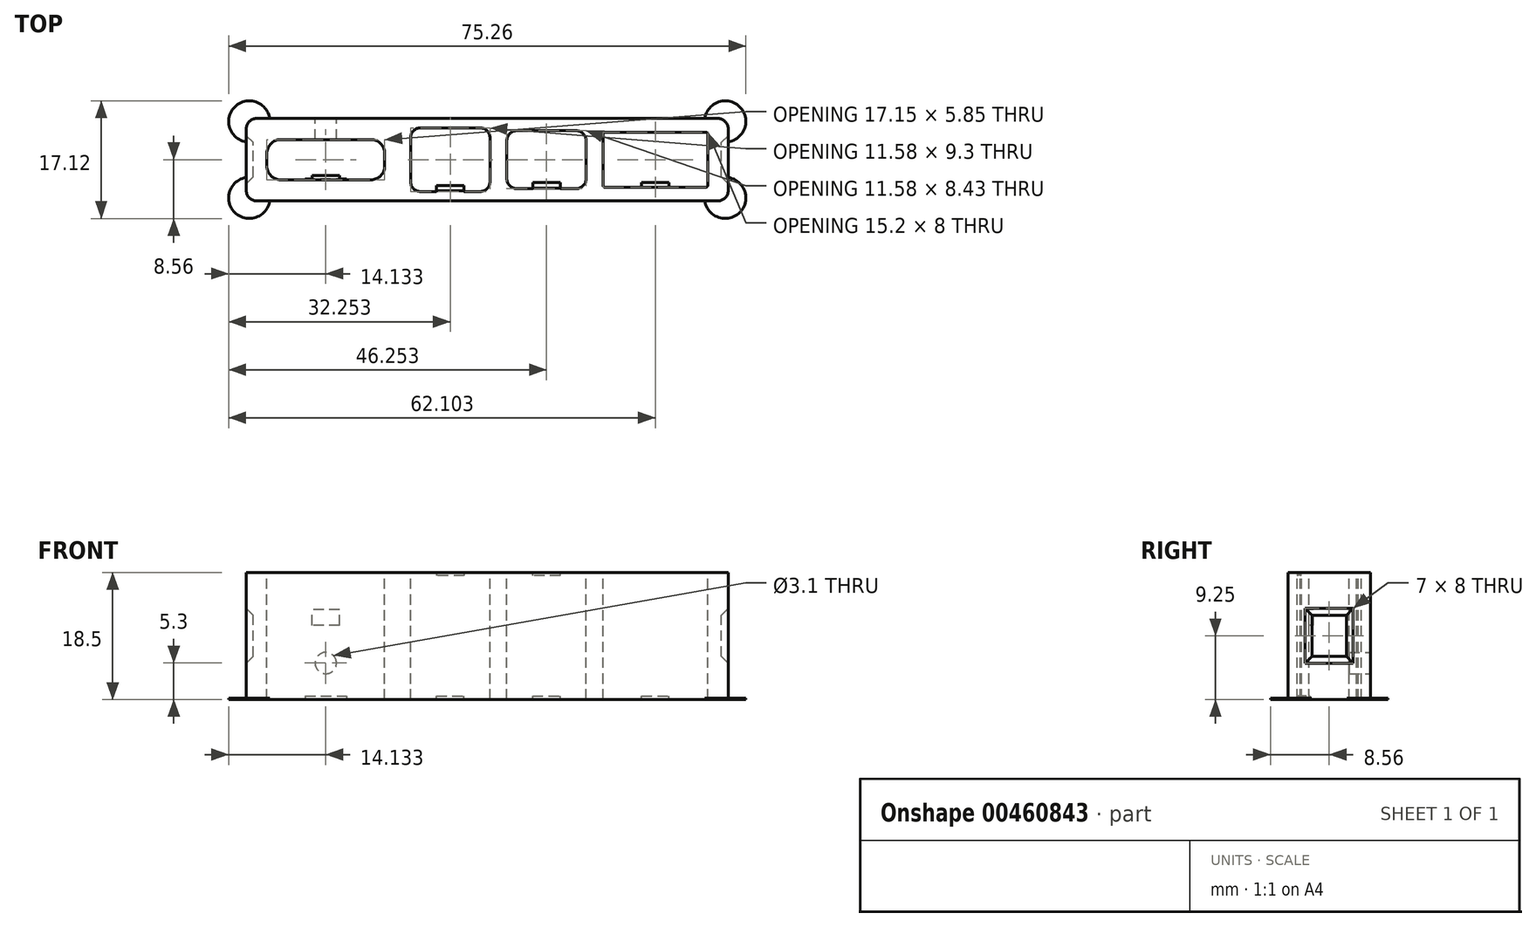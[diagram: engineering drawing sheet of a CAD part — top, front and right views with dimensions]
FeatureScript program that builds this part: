
annotation { "Feature Type Name" : "Feature", "Feature Type Description" : "" }
export const myFeature = defineFeature(function(context is Context, id is Id, definition is map)
    precondition{}
    {
        {
            assignVariable(context, id + "F0", {"name" : "TB1CableStopHeight", "anyValue" : .1});
        }
        {
            var Q0;
            Q0=qCreatedBy(makeId("Front.planeOp"),FACE);
            var sketch = newSketch(context, id + "F1", { "sketchPlane" : qUnion([Q0])});
            skLineSegment(sketch, "E0.bottom", {"start": v(33.57, -6) * mm, "end": v(-33.57, -6) * mm});
            skLineSegment(sketch, "E0.top", {"start": v(33.57, 6) * mm, "end": v(-33.57, 6) * mm});
            skLineSegment(sketch, "E0.left", {"start": v(35.07, -4.5) * mm, "end": v(35.07, 4.5) * mm});
            skLineSegment(sketch, "E0.right", {"start": v(-35.07, -4.5) * mm, "end": v(-35.07, 4.5) * mm});
            skPoint(sketch, "E0.middle", {"position": v(0, 0) * mm});
            skLineSegment(sketch, "E1", {"start": v(-35.07, 0) * mm, "end": v(35.07, 0) * mm, "construction": true});
            skLineSegment(sketch, "E2.bottom", {"start": v(-16.92, -2.92) * mm, "end": v(-30.07, -2.92) * mm});
            skLineSegment(sketch, "E2.top", {"start": v(-16.92, 2.93) * mm, "end": v(-30.07, 2.93) * mm});
            skLineSegment(sketch, "E2.left", {"start": v(-14.92, -0.92) * mm, "end": v(-14.92, 0.93) * mm});
            skLineSegment(sketch, "E2.right", {"start": v(-32.07, -0.92) * mm, "end": v(-32.07, 0.93) * mm});
            skPoint(sketch, "E2.middle", {"position": v(-23.5, 0) * mm});
            skLineSegment(sketch, "E3.bottom", {"start": v(-1.09, 4.65) * mm, "end": v(-9.67, 4.65) * mm});
            skLineSegment(sketch, "E3.top", {"start": v(-1.09, -4.65) * mm, "end": v(-9.67, -4.65) * mm});
            skLineSegment(sketch, "E3.left", {"start": v(0.41, 3.15) * mm, "end": v(0.41, -3.15) * mm});
            skLineSegment(sketch, "E3.right", {"start": v(-11.17, 3.15) * mm, "end": v(-11.17, -3.15) * mm});
            skPoint(sketch, "E3.middle", {"position": v(-5.38, 0) * mm});
            skLineSegment(sketch, "E4.bottom", {"start": v(12.91, 4.21) * mm, "end": v(4.33, 4.21) * mm});
            skLineSegment(sketch, "E4.top", {"start": v(12.91, -4.21) * mm, "end": v(4.33, -4.22) * mm});
            skLineSegment(sketch, "E4.left", {"start": v(14.41, 2.72) * mm, "end": v(14.41, -2.72) * mm});
            skLineSegment(sketch, "E4.right", {"start": v(2.83, 2.71) * mm, "end": v(2.83, -2.72) * mm});
            skPoint(sketch, "E4.middle", {"position": v(8.62, 0) * mm});
            skLineSegment(sketch, "E5.bottom", {"start": v(31.87, -4) * mm, "end": v(17.07, -4) * mm});
            skLineSegment(sketch, "E5.top", {"start": v(31.87, 4) * mm, "end": v(17.07, 4) * mm});
            skLineSegment(sketch, "E5.left", {"start": v(32.07, -3.8) * mm, "end": v(32.07, 3.8) * mm});
            skLineSegment(sketch, "E5.right", {"start": v(16.87, -3.8) * mm, "end": v(16.87, 3.8) * mm});
            skPoint(sketch, "E5.middle", {"position": v(24.47, 0) * mm});
            skPoint(sketch, "E6.visualSharp", {"position": v(-32.07, 2.93) * mm});
            skArc(sketch, "E6.filletArc", {"start": v(-30.07, 2.93) * mm, "mid": v(-31.49, 2.34) * mm, "end": v(-32.07, 0.93) * mm});
            skPoint(sketch, "E7.visualSharp", {"position": v(-14.92, 2.93) * mm});
            skArc(sketch, "E7.filletArc", {"start": v(-14.92, 0.93) * mm, "mid": v(-15.5, 2.34) * mm, "end": v(-16.92, 2.93) * mm});
            skPoint(sketch, "E8.visualSharp", {"position": v(-14.92, -2.92) * mm});
            skArc(sketch, "E8.filletArc", {"start": v(-16.92, -2.92) * mm, "mid": v(-15.5, -2.34) * mm, "end": v(-14.92, -0.92) * mm});
            skPoint(sketch, "E9.visualSharp", {"position": v(-32.07, -2.93) * mm});
            skArc(sketch, "E9.filletArc", {"start": v(-32.07, -0.92) * mm, "mid": v(-31.49, -2.34) * mm, "end": v(-30.07, -2.92) * mm});
            skPoint(sketch, "E10.visualSharp", {"position": v(-11.17, 4.65) * mm});
            skArc(sketch, "E10.filletArc", {"start": v(-9.67, 4.65) * mm, "mid": v(-10.73, 4.21) * mm, "end": v(-11.17, 3.15) * mm});
            skPoint(sketch, "E11.visualSharp", {"position": v(0.41, 4.65) * mm});
            skArc(sketch, "E11.filletArc", {"start": v(0.41, 3.15) * mm, "mid": v(-0.03, 4.21) * mm, "end": v(-1.09, 4.65) * mm});
            skPoint(sketch, "E12.visualSharp", {"position": v(-11.17, -4.65) * mm});
            skArc(sketch, "E12.filletArc", {"start": v(-11.17, -3.15) * mm, "mid": v(-10.73, -4.21) * mm, "end": v(-9.67, -4.65) * mm});
            skPoint(sketch, "E13.visualSharp", {"position": v(0.41, -4.65) * mm});
            skArc(sketch, "E13.filletArc", {"start": v(-1.09, -4.65) * mm, "mid": v(-0.03, -4.21) * mm, "end": v(0.41, -3.15) * mm});
            skPoint(sketch, "E14.visualSharp", {"position": v(2.83, 4.21) * mm});
            skArc(sketch, "E14.filletArc", {"start": v(4.33, 4.21) * mm, "mid": v(3.27, 3.78) * mm, "end": v(2.83, 2.71) * mm});
            skPoint(sketch, "E15.visualSharp", {"position": v(14.41, 4.21) * mm});
            skArc(sketch, "E15.filletArc", {"start": v(14.41, 2.72) * mm, "mid": v(13.97, 3.78) * mm, "end": v(12.91, 4.21) * mm});
            skPoint(sketch, "E16.visualSharp", {"position": v(14.41, -4.21) * mm});
            skArc(sketch, "E16.filletArc", {"start": v(12.91, -4.22) * mm, "mid": v(13.97, -3.78) * mm, "end": v(14.41, -2.72) * mm});
            skPoint(sketch, "E17.visualSharp", {"position": v(2.83, -4.22) * mm});
            skArc(sketch, "E17.filletArc", {"start": v(2.83, -2.72) * mm, "mid": v(3.27, -3.78) * mm, "end": v(4.33, -4.22) * mm});
            skPoint(sketch, "E18.visualSharp", {"position": v(16.87, 4) * mm});
            skArc(sketch, "E18.filletArc", {"start": v(17.07, 4) * mm, "mid": v(16.93, 3.94) * mm, "end": v(16.87, 3.8) * mm});
            skPoint(sketch, "E19.visualSharp", {"position": v(32.07, 4) * mm});
            skArc(sketch, "E19.filletArc", {"start": v(32.07, 3.8) * mm, "mid": v(32.01, 3.94) * mm, "end": v(31.87, 4) * mm});
            skPoint(sketch, "E20.visualSharp", {"position": v(32.07, -4) * mm});
            skArc(sketch, "E20.filletArc", {"start": v(31.87, -4) * mm, "mid": v(32.01, -3.94) * mm, "end": v(32.07, -3.8) * mm});
            skPoint(sketch, "E21.visualSharp", {"position": v(16.87, -4) * mm});
            skArc(sketch, "E21.filletArc", {"start": v(16.87, -3.8) * mm, "mid": v(16.93, -3.94) * mm, "end": v(17.07, -4) * mm});
            skPoint(sketch, "E22.visualSharp", {"position": v(-35.07, 6) * mm});
            skArc(sketch, "E22.filletArc", {"start": v(-33.57, 6) * mm, "mid": v(-34.63, 5.56) * mm, "end": v(-35.07, 4.5) * mm});
            skPoint(sketch, "E23.visualSharp", {"position": v(35.07, 6) * mm});
            skArc(sketch, "E23.filletArc", {"start": v(35.07, 4.5) * mm, "mid": v(34.63, 5.56) * mm, "end": v(33.57, 6) * mm});
            skPoint(sketch, "E24.visualSharp", {"position": v(35.07, -6) * mm});
            skArc(sketch, "E24.filletArc", {"start": v(33.57, -6) * mm, "mid": v(34.63, -5.56) * mm, "end": v(35.07, -4.5) * mm});
            skPoint(sketch, "E25.visualSharp", {"position": v(-35.07, -6) * mm});
            skArc(sketch, "E25.filletArc", {"start": v(-35.07, -4.5) * mm, "mid": v(-34.63, -5.56) * mm, "end": v(-33.57, -6) * mm});
            skSolve(sketch);
        }
        {
            var Q0;
            Q0=makeQuery(id+"F1.imprint","IMPRINT",FACE,{"disambiguationData":[TD([[makeQuery(id+"F1.imprint","IMPRINT",EDGE,{"derivedFrom":sQuery(id+"F1.wireOp",EDGE,"E0.bottom")}),-1.0]])]});
            extrude(context, id + "F2", {"entities" : qUnion([Q0]), "oppositeDirection" : true, "depth" : 18.5 * mm});
        }
        {
            var Q0;
            Q0=makeQuery(id+"F2.opExtrude","SWEPT_FACE",FACE,{"disambiguationData":[OSD([sQuery(id+"F1.wireOp",EDGE,"E0.top")])]});
            var sketch = newSketch(context, id + "F3", { "sketchPlane" : qUnion([Q0])});
            skPoint(sketch, "E26.0", {"position": v(-23.5, 0) * mm});
            skCircle(sketch, "E27", {"center": v(-23.5, 13.2) * mm, "radius": 1.55 * mm});
            skPoint(sketch, "E28.0", {"position": v(33.57, 9.25) * mm});
            skLineSegment(sketch, "E29.bottom", {"start": v(3.5, 13.25) * mm, "end": v(-3.5, 13.25) * mm});
            skLineSegment(sketch, "E29.top", {"start": v(3.5, 5.25) * mm, "end": v(-3.5, 5.25) * mm});
            skLineSegment(sketch, "E29.left", {"start": v(3.5, 13.25) * mm, "end": v(3.5, 5.25) * mm});
            skLineSegment(sketch, "E29.right", {"start": v(-3.5, 13.25) * mm, "end": v(-3.5, 5.25) * mm});
            skPoint(sketch, "E29.middle", {"position": v(0, 9.25) * mm});
            skSolve(sketch);
        }
        {
            var Q0;
            Q0=makeQuery(id+"F3.imprint","IMPRINT",FACE,{"disambiguationData":[TD([[makeQuery(id+"F3.imprint","IMPRINT",EDGE,{"derivedFrom":sQuery(id+"F3.wireOp",EDGE,"E27")}),1.0]])]});
            extrude(context, id + "F4", {"entities" : qUnion([Q0]), "operationType" : NewBodyOperationType.REMOVE, "endBound" : BoundingType.UP_TO_NEXT, "oppositeDirection" : true, "depth" : 25 * mm});
        }
        {
            var Q0;
            Q0=makeQuery(id+"F2.opExtrude","SWEPT_FACE",FACE,{"disambiguationData":[OSD([sQuery(id+"F1.wireOp",EDGE,"E2.bottom")])]});
            var sketch = newSketch(context, id + "F5", { "sketchPlane" : qUnion([Q0])});
            skPoint(sketch, "E30.0", {"position": v(-23.5, 0) * mm});
            skLineSegment(sketch, "E31.bottom", {"start": v(-26.5, 18) * mm, "end": v(-20.5, 18) * mm});
            skLineSegment(sketch, "E31.top", {"start": v(-26.5, 18.5) * mm, "end": v(-20.5, 18.5) * mm});
            skLineSegment(sketch, "E31.left", {"start": v(-26.5, 18) * mm, "end": v(-26.5, 18.5) * mm});
            skLineSegment(sketch, "E31.right", {"start": v(-20.5, 18) * mm, "end": v(-20.5, 18.5) * mm});
            skPoint(sketch, "E31.middle", {"position": v(-23.5, 18.25) * mm});
            skLineSegment(sketch, "E32.0", {"start": v(-16.92, 18.5) * mm, "end": v(-30.07, 18.5) * mm});
            skLineSegment(sketch, "E33.bottom", {"start": v(-21.5, 7.7) * mm, "end": v(-25.5, 7.7) * mm});
            skLineSegment(sketch, "E33.top", {"start": v(-21.5, 5.45) * mm, "end": v(-25.5, 5.45) * mm});
            skLineSegment(sketch, "E33.left", {"start": v(-21.5, 7.7) * mm, "end": v(-21.5, 5.45) * mm});
            skLineSegment(sketch, "E33.right", {"start": v(-25.5, 7.7) * mm, "end": v(-25.5, 5.45) * mm});
            skPoint(sketch, "E33.middle", {"position": v(-23.5, 6.57) * mm});
            skSolve(sketch);
        }
        {
            var Q0;
            Q0=makeQuery(id+"F5.imprint","IMPRINT",FACE,{"disambiguationData":[TD([[makeQuery(id+"F5.imprint","IMPRINT",EDGE,{"derivedFrom":sQuery(id+"F5.wireOp",EDGE,"E31.bottom")}),1.0]])]});
            extrude(context, id + "F6", {"entities" : qUnion([Q0]), "operationType" : NewBodyOperationType.ADD, "depth" : .1 * mm});
        }
        {
            var Q0;
            Q0=makeQuery(id+"F5.imprint","IMPRINT",FACE,{"disambiguationData":[TD([[makeQuery(id+"F5.imprint","IMPRINT",EDGE,{"derivedFrom":sQuery(id+"F5.wireOp",EDGE,"E33.bottom")}),1.0]])]});
            extrude(context, id + "F7", {"entities" : qUnion([Q0]), "operationType" : NewBodyOperationType.ADD, "depth" : .6 * mm});
        }
        {
            var Q0;
            Q0=makeQuery(id+"F2.opExtrude","SWEPT_FACE",FACE,{"disambiguationData":[OSD([sQuery(id+"F1.wireOp",EDGE,"E3.top")])]});
            var sketch = newSketch(context, id + "F8", { "sketchPlane" : qUnion([Q0])});
            skPoint(sketch, "E34.0", {"position": v(-5.38, 0) * mm});
            skLineSegment(sketch, "E35.bottom", {"start": v(-7.38, 18.5) * mm, "end": v(-3.38, 18.5) * mm});
            skLineSegment(sketch, "E35.top", {"start": v(-7.38, 18) * mm, "end": v(-3.38, 18) * mm});
            skLineSegment(sketch, "E35.left", {"start": v(-7.38, 18.5) * mm, "end": v(-7.38, 18) * mm});
            skLineSegment(sketch, "E35.right", {"start": v(-3.38, 18.5) * mm, "end": v(-3.38, 18) * mm});
            skPoint(sketch, "E35.middle", {"position": v(-5.38, 18.25) * mm});
            skLineSegment(sketch, "E36.bottom", {"start": v(-3.38, -1.03) * mm, "end": v(-7.38, -1.03) * mm});
            skLineSegment(sketch, "E36.top", {"start": v(-3.38, 0.47) * mm, "end": v(-7.38, 0.47) * mm});
            skLineSegment(sketch, "E36.left", {"start": v(-3.38, -1.03) * mm, "end": v(-3.38, 0.47) * mm});
            skLineSegment(sketch, "E36.right", {"start": v(-7.38, -1.03) * mm, "end": v(-7.38, 0.47) * mm});
            skPoint(sketch, "E36.middle", {"position": v(-5.38, -0.28) * mm});
            skLineSegment(sketch, "E37.0", {"start": v(-1.09, 18.5) * mm, "end": v(-9.67, 18.5) * mm});
            skSolve(sketch);
        }
        {
            var Q0;
            Q0=makeQuery(id+"F8.imprint","IMPRINT",FACE,{"disambiguationData":[TD([[makeQuery(id+"F8.imprint","IMPRINT",EDGE,{"derivedFrom":sQuery(id+"F8.wireOp",EDGE,"E35.top")}),1.0]])]});
            extrude(context, id + "F9", {"entities" : qUnion([Q0]), "operationType" : NewBodyOperationType.ADD, "depth" : .9 * mm});
        }
        {
            var Q0;
            {var subQ0=sQuery(id+"F8.wireOp",EDGE,"E36.top");Q0=makeQuery(id+"F8.imprint","IMPRINT",FACE,{"disambiguationData":[TD([[makeQuery(id+"F8.imprint","IMPRINT",EDGE,{"derivedFrom":subQ0}),1.0]])]});}
            extrude(context, id + "F10", {"entities" : qUnion([Q0]), "operationType" : NewBodyOperationType.ADD, "depth" : (getVariable(context, 'TB1CableStopHeight')) * mm});
        }
        {
            var Q0;
            Q0=makeQuery(id+"F2.opExtrude","SWEPT_FACE",FACE,{"disambiguationData":[OSD([sQuery(id+"F1.wireOp",EDGE,"E4.top")])]});
            var sketch = newSketch(context, id + "F11", { "sketchPlane" : qUnion([Q0])});
            skPoint(sketch, "E38.0", {"position": v(8.62, 0) * mm});
            skLineSegment(sketch, "E39.bottom", {"start": v(6.62, 18.5) * mm, "end": v(10.62, 18.5) * mm});
            skLineSegment(sketch, "E39.top", {"start": v(6.62, 18) * mm, "end": v(10.62, 18) * mm});
            skLineSegment(sketch, "E39.left", {"start": v(6.62, 18.5) * mm, "end": v(6.62, 18) * mm});
            skLineSegment(sketch, "E39.right", {"start": v(10.62, 18.5) * mm, "end": v(10.62, 18) * mm});
            skPoint(sketch, "E39.middle", {"position": v(8.62, 18.25) * mm});
            skLineSegment(sketch, "E40.bottom", {"start": v(10.62, 0.47) * mm, "end": v(6.62, 0.47) * mm});
            skLineSegment(sketch, "E40.top", {"start": v(10.62, -1.03) * mm, "end": v(6.62, -1.03) * mm});
            skLineSegment(sketch, "E40.left", {"start": v(10.62, 0.47) * mm, "end": v(10.62, -1.03) * mm});
            skLineSegment(sketch, "E40.right", {"start": v(6.62, 0.47) * mm, "end": v(6.62, -1.03) * mm});
            skPoint(sketch, "E40.middle", {"position": v(8.62, -0.28) * mm});
            skLineSegment(sketch, "E41.0", {"start": v(12.91, 18.5) * mm, "end": v(4.33, 18.5) * mm});
            skSolve(sketch);
        }
        {
            var Q0;
            Q0=makeQuery(id+"F11.imprint","IMPRINT",FACE,{"disambiguationData":[TD([[makeQuery(id+"F11.imprint","IMPRINT",EDGE,{"derivedFrom":sQuery(id+"F11.wireOp",EDGE,"E39.top")}),1.0]])]});
            extrude(context, id + "F12", {"entities" : qUnion([Q0]), "operationType" : NewBodyOperationType.ADD, "depth" : .9 * mm});
        }
        {
            var Q0;
            Q0=makeQuery(id+"F11.imprint","IMPRINT",FACE,{"disambiguationData":[TD([[makeQuery(id+"F11.imprint","IMPRINT",EDGE,{"derivedFrom":sQuery(id+"F11.wireOp",EDGE,"E40.bottom")}),1.0]])]});
            extrude(context, id + "F13", {"entities" : qUnion([Q0]), "operationType" : NewBodyOperationType.ADD, "depth" : (getVariable(context, 'TB1CableStopHeight')) * mm});
        }
        {
            var Q0;
            Q0=makeQuery(id+"F2.opExtrude","SWEPT_FACE",FACE,{"disambiguationData":[OSD([sQuery(id+"F1.wireOp",EDGE,"E5.bottom")])]});
            var sketch = newSketch(context, id + "F14", { "sketchPlane" : qUnion([Q0])});
            skPoint(sketch, "E42.0", {"position": v(24.47, 0) * mm});
            skLineSegment(sketch, "E43.bottom", {"start": v(22.47, 18.5) * mm, "end": v(26.47, 18.5) * mm});
            skLineSegment(sketch, "E43.top", {"start": v(22.47, 18) * mm, "end": v(26.47, 18) * mm});
            skLineSegment(sketch, "E43.left", {"start": v(22.47, 18.5) * mm, "end": v(22.47, 18) * mm});
            skLineSegment(sketch, "E43.right", {"start": v(26.47, 18.5) * mm, "end": v(26.47, 18) * mm});
            skPoint(sketch, "E43.middle", {"position": v(24.47, 18.25) * mm});
            skSolve(sketch);
        }
        {
            var Q0;
            Q0=makeQuery(id+"F14.imprint","IMPRINT",FACE,{"disambiguationData":[TD([[makeQuery(id+"F14.imprint","IMPRINT",EDGE,{"derivedFrom":sQuery(id+"F14.wireOp",EDGE,"E43.bottom")}),1.0]])]});
            extrude(context, id + "F15", {"entities" : qUnion([Q0]), "operationType" : NewBodyOperationType.ADD, "depth" : .7 * mm});
        }
        {
            var Q0;
            Q0=makeQuery(id+"F2.opExtrude","SWEPT_FACE",FACE,{"disambiguationData":[OSD([sQuery(id+"F1.wireOp",EDGE,"E0.left")])]});
            var sketch = newSketch(context, id + "F16", { "sketchPlane" : qUnion([Q0])});
            skPoint(sketch, "E44.0", {"position": v(9.25, 6) * mm});
            skPoint(sketch, "E45.0", {"position": v(18.5, 0) * mm});
            skLineSegment(sketch, "E46.bottom", {"start": v(13.25, 3.5) * mm, "end": v(5.25, 3.5) * mm});
            skLineSegment(sketch, "E46.top", {"start": v(13.25, -3.5) * mm, "end": v(5.25, -3.5) * mm});
            skLineSegment(sketch, "E46.left", {"start": v(13.25, 3.5) * mm, "end": v(13.25, -3.5) * mm});
            skLineSegment(sketch, "E46.right", {"start": v(5.25, 3.5) * mm, "end": v(5.25, -3.5) * mm});
            skPoint(sketch, "E46.middle", {"position": v(9.25, 0) * mm});
            skSolve(sketch);
        }
        {
            var Q0;
            Q0=qSketchRegion(id+"F16",true);
            extrude(context, id + "F17", {"entities" : qUnion([Q0]), "operationType" : NewBodyOperationType.REMOVE, "oppositeDirection" : true, "depth" : 1 * mm, "hasDraft" : true, "draftAngle" : 45 * degree, "draftPullDirection" : true});
        }
        {
            var Q0;
            Q0=makeQuery(id+"F2.opExtrude","SWEPT_FACE",FACE,{"disambiguationData":[OSD([sQuery(id+"F1.wireOp",EDGE,"E0.right")])]});
            var sketch = newSketch(context, id + "F18", { "sketchPlane" : qUnion([Q0])});
            skPoint(sketch, "E47.0", {"position": v(-9.25, 6) * mm});
            skPoint(sketch, "E48.0", {"position": v(0, 0) * mm});
            skLineSegment(sketch, "E49.bottom", {"start": v(-5.25, -3.5) * mm, "end": v(-13.25, -3.5) * mm});
            skLineSegment(sketch, "E49.top", {"start": v(-5.25, 3.5) * mm, "end": v(-13.25, 3.5) * mm});
            skLineSegment(sketch, "E49.left", {"start": v(-5.25, -3.5) * mm, "end": v(-5.25, 3.5) * mm});
            skLineSegment(sketch, "E49.right", {"start": v(-13.25, -3.5) * mm, "end": v(-13.25, 3.5) * mm});
            skPoint(sketch, "E49.middle", {"position": v(-9.25, 0) * mm});
            skSolve(sketch);
        }
        {
            var Q0;
            Q0=qSketchRegion(id+"F18",true);
            extrude(context, id + "F19", {"entities" : qUnion([Q0]), "operationType" : NewBodyOperationType.REMOVE, "oppositeDirection" : true, "depth" : 1 * mm, "hasDraft" : true, "draftAngle" : 45 * degree, "draftPullDirection" : true});
        }
        {
            var Q0;
            Q0=makeQuery(id+"F2.opExtrude","SWEPT_FACE",FACE,{"disambiguationData":[OSD([sQuery(id+"F1.wireOp",EDGE,"E0.bottom")])]});
            var sketch = newSketch(context, id + "F20", { "sketchPlane" : qUnion([Q0])});
            skPoint(sketch, "E50.0", {"position": v(-38.78, -17.75) * mm});
            skPoint(sketch, "E51.0", {"position": v(0, 0) * mm});
            skPoint(sketch, "E52.0", {"position": v(33.57, -9.25) * mm});
            skLineSegment(sketch, "E53.bottom", {"start": v(4, -5.75) * mm, "end": v(-4, -5.75) * mm});
            skLineSegment(sketch, "E53.top", {"start": v(4, -12.75) * mm, "end": v(-4, -12.75) * mm});
            skLineSegment(sketch, "E53.left", {"start": v(4, -5.75) * mm, "end": v(4, -12.75) * mm});
            skLineSegment(sketch, "E53.right", {"start": v(-4, -5.75) * mm, "end": v(-4, -12.75) * mm});
            skPoint(sketch, "E53.middle", {"position": v(0, -9.25) * mm});
            skText(sketch, "E54", { "text": "JS", "fontName": "OpenSans-Regular.ttf"});
            const initialGuessF20  = {"E54": [0.0279, -0.01727, 1, 0, 0.00333]};
            skSetInitialGuess(sketch, initialGuessF20);
            skSolve(sketch);
        }
        {
            var Q0;
            Q0=makeQuery(id+"F15.boolean.opBoolean","MERGE",FACE,{"derivedFrom":[makeQuery(id+"F12.boolean.opBoolean","MERGE",FACE,{"derivedFrom":[makeQuery(id+"F9.boolean.opBoolean","MERGE",FACE,{"derivedFrom":[makeQuery(id+"F6.boolean.opBoolean","MERGE",FACE,{"derivedFrom":[makeQuery(id+"F2.opExtrude","CAP_FACE",FACE,{"disambiguationData":[OSD([sQuery(id+"F1.wireOp",EDGE,"E0.bottom"),sQuery(id+"F1.wireOp",EDGE,"E0.top"),sQuery(id+"F1.wireOp",EDGE,"E0.left"),sQuery(id+"F1.wireOp",EDGE,"E0.right"),sQuery(id+"F1.wireOp",EDGE,"E2.bottom"),sQuery(id+"F1.wireOp",EDGE,"E2.top"),sQuery(id+"F1.wireOp",EDGE,"E2.left"),sQuery(id+"F1.wireOp",EDGE,"E2.right"),sQuery(id+"F1.wireOp",EDGE,"E3.bottom"),sQuery(id+"F1.wireOp",EDGE,"E3.top"),sQuery(id+"F1.wireOp",EDGE,"E3.left"),sQuery(id+"F1.wireOp",EDGE,"E3.right"),sQuery(id+"F1.wireOp",EDGE,"E4.bottom"),sQuery(id+"F1.wireOp",EDGE,"E4.top"),sQuery(id+"F1.wireOp",EDGE,"E4.left"),sQuery(id+"F1.wireOp",EDGE,"E4.right"),sQuery(id+"F1.wireOp",EDGE,"E5.bottom"),sQuery(id+"F1.wireOp",EDGE,"E5.top"),sQuery(id+"F1.wireOp",EDGE,"E5.left"),sQuery(id+"F1.wireOp",EDGE,"E5.right"),sQuery(id+"F1.wireOp",EDGE,"E6.filletArc"),sQuery(id+"F1.wireOp",EDGE,"E7.filletArc"),sQuery(id+"F1.wireOp",EDGE,"E8.filletArc"),sQuery(id+"F1.wireOp",EDGE,"E9.filletArc"),sQuery(id+"F1.wireOp",EDGE,"E10.filletArc"),sQuery(id+"F1.wireOp",EDGE,"E11.filletArc"),sQuery(id+"F1.wireOp",EDGE,"E12.filletArc"),sQuery(id+"F1.wireOp",EDGE,"E13.filletArc"),sQuery(id+"F1.wireOp",EDGE,"E14.filletArc"),sQuery(id+"F1.wireOp",EDGE,"E15.filletArc"),sQuery(id+"F1.wireOp",EDGE,"E16.filletArc"),sQuery(id+"F1.wireOp",EDGE,"E17.filletArc"),sQuery(id+"F1.wireOp",EDGE,"E18.filletArc"),sQuery(id+"F1.wireOp",EDGE,"E19.filletArc"),sQuery(id+"F1.wireOp",EDGE,"E20.filletArc"),sQuery(id+"F1.wireOp",EDGE,"E21.filletArc"),sQuery(id+"F1.wireOp",EDGE,"E22.filletArc"),sQuery(id+"F1.wireOp",EDGE,"E23.filletArc"),sQuery(id+"F1.wireOp",EDGE,"E24.filletArc"),sQuery(id+"F1.wireOp",EDGE,"E25.filletArc")])],"isStart":false}),makeQuery(id+"F6.opExtrude","SWEPT_FACE",FACE,{"disambiguationData":[OSD([sQuery(id+"F5.wireOp",EDGE,"E32.0")])]})]}),makeQuery(id+"F9.opExtrude","SWEPT_FACE",FACE,{"disambiguationData":[OSD([sQuery(id+"F8.wireOp",EDGE,"E37.0")])]})]}),makeQuery(id+"F12.opExtrude","SWEPT_FACE",FACE,{"disambiguationData":[OSD([sQuery(id+"F11.wireOp",EDGE,"E41.0")])]})]}),makeQuery(id+"F15.opExtrude","SWEPT_FACE",FACE,{"disambiguationData":[OSD([sQuery(id+"F14.wireOp",EDGE,"E43.bottom")])]})]});
            var sketch = newSketch(context, id + "F21", { "sketchPlane" : qUnion([Q0])});
            skCircle(sketch, "E55", {"center": v(-34.63, 5.56) * mm, "radius": 3 * mm});
            skCircle(sketch, "E56", {"center": v(34.63, 5.56) * mm, "radius": 3 * mm});
            skCircle(sketch, "E57", {"center": v(34.63, -5.56) * mm, "radius": 3 * mm});
            skCircle(sketch, "E58", {"center": v(-34.63, -5.56) * mm, "radius": 3 * mm});
            skSolve(sketch);
        }
        {
            var Q0;
            {var subQ5=makeQuery(id+"F2.opExtrude","CAP_EDGE",EDGE,{"disambiguationData":[OSD([sQuery(id+"F1.wireOp",EDGE,"E23.filletArc")])],"isStart":false});Q0=makeQuery(id+"F21.imprint","IMPRINT",FACE,{"disambiguationData":[TD([[makeQuery(id+"F21.imprint","IMPRINT",EDGE,{"derivedFrom":subQ5}),1.0]])]});}
            var Q1;
            {var subQ5=makeQuery(id+"F2.opExtrude","CAP_EDGE",EDGE,{"disambiguationData":[OSD([sQuery(id+"F1.wireOp",EDGE,"E24.filletArc")])],"isStart":false});Q1=makeQuery(id+"F21.imprint","IMPRINT",FACE,{"disambiguationData":[TD([[makeQuery(id+"F21.imprint","IMPRINT",EDGE,{"derivedFrom":subQ5}),1.0]])]});}
            var Q2;
            {var subQ5=makeQuery(id+"F2.opExtrude","CAP_EDGE",EDGE,{"disambiguationData":[OSD([sQuery(id+"F1.wireOp",EDGE,"E22.filletArc")])],"isStart":false});Q2=makeQuery(id+"F21.imprint","IMPRINT",FACE,{"disambiguationData":[TD([[makeQuery(id+"F21.imprint","IMPRINT",EDGE,{"derivedFrom":subQ5}),1.0]])]});}
            var Q3;
            {var subQ5=makeQuery(id+"F2.opExtrude","CAP_EDGE",EDGE,{"disambiguationData":[OSD([sQuery(id+"F1.wireOp",EDGE,"E25.filletArc")])],"isStart":false});Q3=makeQuery(id+"F21.imprint","IMPRINT",FACE,{"disambiguationData":[TD([[makeQuery(id+"F21.imprint","IMPRINT",EDGE,{"derivedFrom":subQ5}),1.0]])]});}
            extrude(context, id + "F22", {"entities" : qUnion([Q0, Q1, Q2, Q3]), "operationType" : NewBodyOperationType.ADD, "oppositeDirection" : true, "depth" : .2 * mm});
        }
        {
            var Q0;
            Q0=makeQuery(id+"F2.opExtrude","SWEPT_BODY",BODY,{"disambiguationData":[OSD([sQuery(id+"F1.wireOp",EDGE,"E0.bottom"),sQuery(id+"F1.wireOp",EDGE,"E0.top"),sQuery(id+"F1.wireOp",EDGE,"E0.left"),sQuery(id+"F1.wireOp",EDGE,"E0.right"),sQuery(id+"F1.wireOp",EDGE,"E2.bottom"),sQuery(id+"F1.wireOp",EDGE,"E2.top"),sQuery(id+"F1.wireOp",EDGE,"E2.left"),sQuery(id+"F1.wireOp",EDGE,"E2.right"),sQuery(id+"F1.wireOp",EDGE,"E3.bottom"),sQuery(id+"F1.wireOp",EDGE,"E3.top"),sQuery(id+"F1.wireOp",EDGE,"E3.left"),sQuery(id+"F1.wireOp",EDGE,"E3.right"),sQuery(id+"F1.wireOp",EDGE,"E4.bottom"),sQuery(id+"F1.wireOp",EDGE,"E4.top"),sQuery(id+"F1.wireOp",EDGE,"E4.left"),sQuery(id+"F1.wireOp",EDGE,"E4.right"),sQuery(id+"F1.wireOp",EDGE,"E5.bottom"),sQuery(id+"F1.wireOp",EDGE,"E5.top"),sQuery(id+"F1.wireOp",EDGE,"E5.left"),sQuery(id+"F1.wireOp",EDGE,"E5.right"),sQuery(id+"F1.wireOp",EDGE,"E6.filletArc"),sQuery(id+"F1.wireOp",EDGE,"E7.filletArc"),sQuery(id+"F1.wireOp",EDGE,"E8.filletArc"),sQuery(id+"F1.wireOp",EDGE,"E9.filletArc"),sQuery(id+"F1.wireOp",EDGE,"E10.filletArc"),sQuery(id+"F1.wireOp",EDGE,"E11.filletArc"),sQuery(id+"F1.wireOp",EDGE,"E12.filletArc"),sQuery(id+"F1.wireOp",EDGE,"E13.filletArc"),sQuery(id+"F1.wireOp",EDGE,"E14.filletArc"),sQuery(id+"F1.wireOp",EDGE,"E15.filletArc"),sQuery(id+"F1.wireOp",EDGE,"E16.filletArc"),sQuery(id+"F1.wireOp",EDGE,"E17.filletArc"),sQuery(id+"F1.wireOp",EDGE,"E18.filletArc"),sQuery(id+"F1.wireOp",EDGE,"E19.filletArc"),sQuery(id+"F1.wireOp",EDGE,"E20.filletArc"),sQuery(id+"F1.wireOp",EDGE,"E21.filletArc"),sQuery(id+"F1.wireOp",EDGE,"E22.filletArc"),sQuery(id+"F1.wireOp",EDGE,"E23.filletArc"),sQuery(id+"F1.wireOp",EDGE,"E24.filletArc"),sQuery(id+"F1.wireOp",EDGE,"E25.filletArc")])]});
            var Q1;
            Q1=makeQuery(id+"F2.opExtrude","CAP_EDGE",EDGE,{"disambiguationData":[OSD([sQuery(id+"F1.wireOp",EDGE,"E0.top")])],"isStart":false});
            transform(context, id + "F23", {"entities" : qUnion([Q0]), "transformType" : TransformType.ROTATION, "transformAxis" : qUnion([Q1]), "angle" : 90 * degree, "makeCopy" : false});
        }
    });
